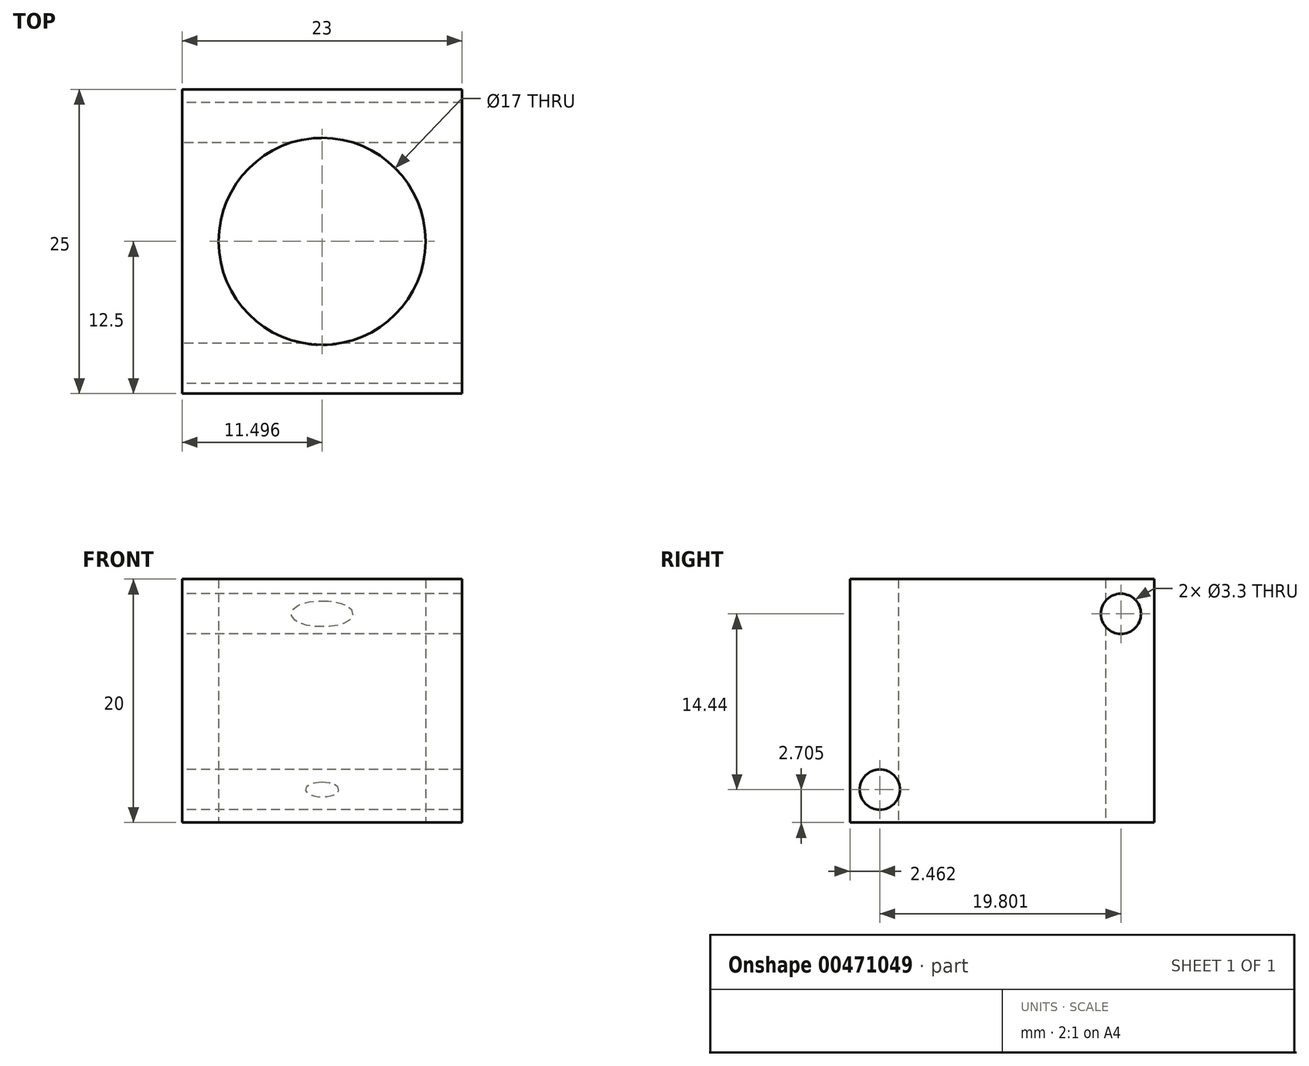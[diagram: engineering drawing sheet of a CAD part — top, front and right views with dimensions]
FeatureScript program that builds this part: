
annotation { "Feature Type Name" : "Feature", "Feature Type Description" : "" }
export const myFeature = defineFeature(function(context is Context, id is Id, definition is map)
    precondition{}
    {
        {
            var Q0;
            Q0=qCreatedBy(makeId("Top.planeOp"),FACE);
            var sketch = newSketch(context, id + "F0", { "sketchPlane" : qUnion([Q0])});
            skLineSegment(sketch, "E0.bottom", {"start": v(-35.85, 25) * mm, "end": v(-12.85, 25) * mm});
            skLineSegment(sketch, "E0.top", {"start": v(-35.85, 0) * mm, "end": v(-12.85, 0) * mm});
            skLineSegment(sketch, "E0.left", {"start": v(-35.85, 25) * mm, "end": v(-35.85, 0) * mm});
            skLineSegment(sketch, "E0.right", {"start": v(-12.85, 25) * mm, "end": v(-12.85, 0) * mm});
            skCircle(sketch, "E1", {"center": v(-24.35, 12.5) * mm, "radius": 8.5 * mm});
            skSolve(sketch);
        }
        {
            var Q0;
            Q0 = qSketchRegion(id + "F0", true);
            extrude(context, id + "F1", {"entities" : qUnion([Q0]), "depth" : 20 * mm, "offsetDistance" : 25 * mm});
        }
        {
            var Q0;
            Q0=makeQuery(id+"F1.opExtrude","SWEPT_FACE",FACE,{"disambiguationData":[OSD([sQuery(id+"F0.wireOp",EDGE,"E0.left")])]});
            var sketch = newSketch(context, id + "F2", { "sketchPlane" : qUnion([Q0])});
            skCircle(sketch, "E2", {"center": v(-2.46, 2.7) * mm, "radius": 1.65 * mm});
            skCircle(sketch, "E3", {"center": v(-22.26, 17.14) * mm, "radius": 1.65 * mm});
            skSolve(sketch);
        }
        {
            var Q0;
            Q0=sQuery(id+"F2.wireOp",VERTEX,"E2.center");
            var Q1;
            Q1=sQuery(id+"F2.wireOp",VERTEX,"E3.center");
            var Q2;
            Q2=sQuery(id+"F2.wireOp",VERTEX,"E3.center");
            var Q3;
            Q3=makeQuery(id+"F1.opExtrude","SWEPT_BODY",BODY,{"disambiguationData":[OSD([sQuery(id+"F0.wireOp",EDGE,"E0.bottom"),sQuery(id+"F0.wireOp",EDGE,"E0.top"),sQuery(id+"F0.wireOp",EDGE,"E0.left"),sQuery(id+"F0.wireOp",EDGE,"E0.right"),sQuery(id+"F0.wireOp",EDGE,"E1")])]});
            hole(context, id + "F3", {"style" : HoleStyle.SIMPLE, "endStyle" : HoleEndStyle.THROUGH, "holeDiameter" : 3.3 * mm, "isTappedThrough" : true, "tappedDepth" : 12 * mm, "tapClearance" : 3, "locations" : qUnion([Q0, Q1, Q2]), "scope" : qUnion([Q3])});
        }
    });
